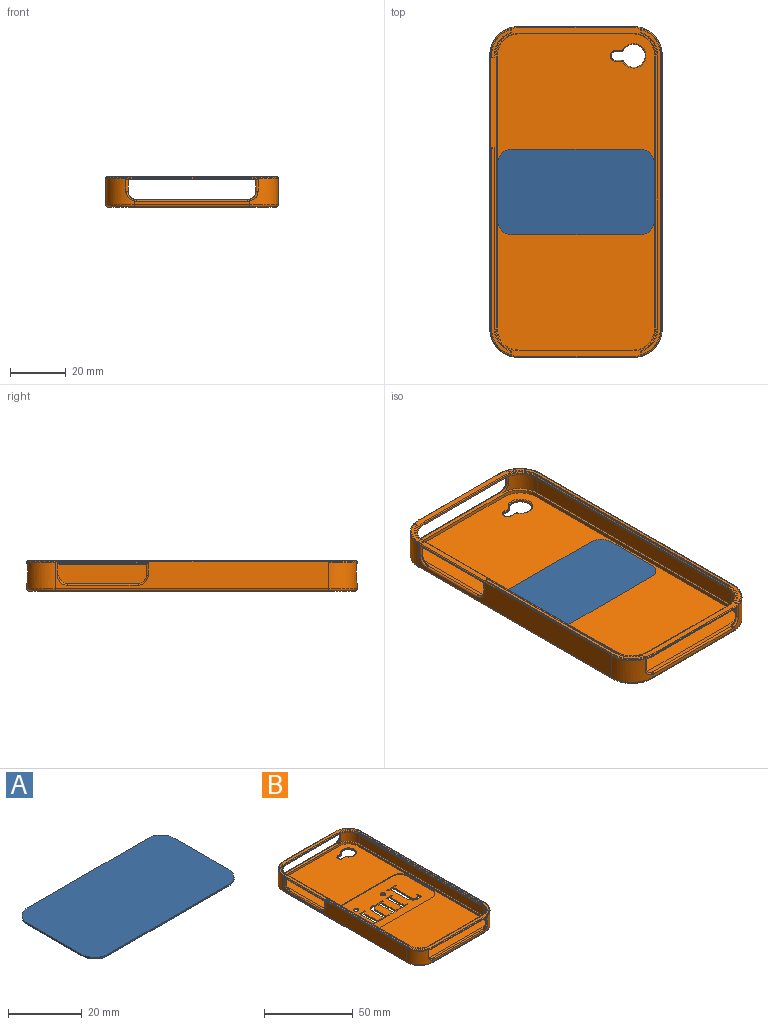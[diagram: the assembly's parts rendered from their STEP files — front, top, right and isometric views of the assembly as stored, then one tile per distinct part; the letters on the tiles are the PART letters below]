
ASSEMBLY  parts=2 mates=1
PART A: 94 faces, bbox 56.3x30.7x1.5 mm
  f0: plane 20.75x0.5mm, normal (-1,0,0), area 10.4mm2, adj f1,f7,f8,f9
  f1: cylinder r=5mm len=5mm, axis (0,0,-1), area 3.9mm2, adj f0,f2,f8,f9
  f2: plane 46.31x0.5mm, normal (0,-1,0), area 23.2mm2, adj f1,f3,f8,f9
  f3: cylinder r=5mm len=5mm, axis (0,0,-1), area 3.9mm2, adj f2,f4,f8,f9
  f4: plane 20.75x0.5mm, normal (1,0,0), area 10.4mm2, adj f3,f5,f8,f9
  f5: cylinder r=5mm len=5mm, axis (0,0,-1), area 3.9mm2, adj f4,f6,f8,f9
  f6: plane 46.31x0.5mm, normal (0,1,0), area 23.2mm2, adj f5,f7,f8,f9
  f7: cylinder r=5mm len=5mm, axis (0,0,-1), area 3.9mm2, adj f0,f6,f8,f9
  f8: plane 56.31x30.75mm, normal (0,0,1), area 1710.1mm2, adj f0,f1,f2,f3,f4,f5,f6,f7
  f9: plane 56.31x30.75mm, normal (0,0,-1), area 1506.8mm2, adj f0,f1,f2,f3,f4,f5,f6,f7
  f10: plane 2.31x1mm, normal (0.15,-0.99,0), area 2.3mm2, adj f9,f11,f26,f27
  f11: plane 13.54x1mm, normal (1,0,0), area 13.5mm2, adj f9,f10,f12,f27
  f12: extruded ~2.56x1.88mm, area 3.6mm2, adj f9,f11,f13,f27
  f13: extruded ~1.04x1mm, area 1.1mm2, adj f9,f12,f14,f27
  f14: extruded ~1x0.73mm, area 0.9mm2, adj f9,f13,f15,f27
  f15: plane 1.87x1mm, normal (-0.98,0.21,0), area 1.9mm2, adj f9,f14,f16,f27
  f16: plane 1x0.89mm, normal (0,1,0), area 0.9mm2, adj f9,f15,f17,f27
  f17: plane 3.29x1mm, normal (1,0,0), area 3.3mm2, adj f9,f16,f18,f27
  f18: extruded ~2.79x1mm, area 2.8mm2, adj f9,f17,f19,f27
  f19: extruded ~2.51x1mm, area 2.7mm2, adj f9,f18,f20,f27
  f20: extruded ~2.14x1.68mm, area 2.8mm2, adj f9,f19,f21,f27
  f21: extruded ~3.16x1mm, area 3.2mm2, adj f9,f20,f22,f27
  f22: plane 11.17x1mm, normal (-1,0,0), area 11.2mm2, adj f9,f21,f23,f27
  f23: plane 2.05x1mm, normal (-0.17,-0.99,0), area 2.1mm2, adj f9,f22,f24,f27
  f24: plane 1x0.72mm, normal (-1,0,0), area 0.7mm2, adj f9,f23,f25,f27
  f25: plane 6.94x1mm, normal (0,1,0), area 6.9mm2, adj f9,f24,f26,f27
  f26: plane 1x0.72mm, normal (1,0,0), area 0.7mm2, adj f9,f10,f25,f27
  f27: plane 18.32x9.57mm, normal (0,0,-1), area 55.1mm2, adj f10,f11,f12,f13,f14,f15,f16,f17
  f28: extruded ~1.03x1mm, area 1.1mm2, adj f9,f29,f35,f36
  f29: extruded ~1.04x1mm, area 1.2mm2, adj f9,f28,f30,f36
  f30: extruded ~1.03x1mm, area 1.2mm2, adj f9,f29,f31,f36
  f31: extruded ~1.03x1mm, area 1.1mm2, adj f9,f30,f32,f36
  f32: extruded ~1.04x1mm, area 1.2mm2, adj f9,f31,f33,f36
  f33: extruded ~1.03x1mm, area 1.1mm2, adj f9,f32,f34,f36
  f34: extruded ~1.03x1mm, area 1.1mm2, adj f9,f33,f35,f36
  f35: extruded ~1.03x1mm, area 1.2mm2, adj f9,f28,f34,f36
  f36: plane 2.92x2.92mm, normal (0,0,-1), area 6.7mm2, adj f28,f29,f30,f31,f32,f33,f34,f35
  f37: plane 2.17x1mm, normal (-0.15,0.99,0), area 2.2mm2, adj f9,f38,f46,f47
  f38: plane 11.71x1mm, normal (-1,0,0), area 11.7mm2, adj f9,f37,f39,f47
  f39: plane 4.02x1mm, normal (0,1,0), area 4mm2, adj f9,f38,f40,f47
  f40: plane 1x0.61mm, normal (1,0,0), area 0.6mm2, adj f9,f39,f41,f47
  f41: plane 1.79x1mm, normal (0.18,-0.98,0), area 1.8mm2, adj f9,f40,f42,f47
  f42: plane 10.77x1mm, normal (1,0,0), area 10.8mm2, adj f9,f41,f43,f47
  f43: plane 2.15x1mm, normal (0.15,0.99,0), area 2.2mm2, adj f9,f42,f44,f47
  f44: plane 1x0.61mm, normal (1,0,0), area 0.6mm2, adj f9,f43,f45,f47
  f45: plane 6.55x1mm, normal (0,-1,0), area 6.6mm2, adj f9,f44,f46,f47
  f46: plane 1x0.61mm, normal (-1,0,0), area 0.6mm2, adj f9,f37,f45,f47
  f47: plane 12.65x6.55mm, normal (0,0,-1), area 33mm2, adj f37,f38,f39,f40,f41,f42,f43,f44
  f48: extruded ~2.21x1mm, area 2.4mm2, adj f9,f49,f72,f73
  f49: plane 1.03x1mm, normal (-0.99,0.12,0), area 1mm2, adj f9,f48,f50,f73
  f50: plane 3.6x1mm, normal (0,1,0), area 3.6mm2, adj f9,f49,f51,f73
  f51: plane 1x0.61mm, normal (1,0,0), area 0.6mm2, adj f9,f50,f52,f73
  f52: plane 1.52x1mm, normal (0.22,-0.98,0), area 1.6mm2, adj f9,f51,f53,f73
  f53: plane 10.77x1mm, normal (1,0,0), area 10.8mm2, adj f9,f52,f54,f73
  f54: plane 1.52x1mm, normal (0.22,0.98,0), area 1.6mm2, adj f9,f53,f55,f73
  f55: plane 1x0.61mm, normal (1,0,0), area 0.6mm2, adj f9,f54,f56,f73
  f56: plane 5.46x1mm, normal (0,-1,0), area 5.5mm2, adj f9,f55,f57,f73
  f57: plane 1x0.61mm, normal (-1,0,0), area 0.6mm2, adj f9,f56,f58,f73
  f58: plane 1.71x1mm, normal (-0.19,0.98,0), area 1.7mm2, adj f9,f57,f59,f73
  f59: plane 10.08x1mm, normal (-1,0,0), area 10.1mm2, adj f9,f58,f60,f73
  f60: extruded ~2.97x1mm, area 3mm2, adj f9,f59,f61,f73
  f61: extruded ~1.69x1mm, area 1.9mm2, adj f9,f60,f62,f73
  f62: extruded ~1.76x1mm, area 1.9mm2, adj f9,f61,f63,f73
  f63: plane 8.07x1mm, normal (1,0,0), area 8.1mm2, adj f9,f62,f64,f73
  f64: plane 1.68x1mm, normal (0.2,0.98,0), area 1.7mm2, adj f9,f63,f65,f73
  f65: plane 1x0.61mm, normal (1,0,0), area 0.6mm2, adj f9,f64,f66,f73
  f66: plane 5.45x1mm, normal (0,-1,0), area 5.4mm2, adj f9,f65,f67,f73
  f67: plane 1x0.61mm, normal (-1,0,0), area 0.6mm2, adj f9,f66,f68,f73
  f68: plane 1.53x1mm, normal (-0.21,0.98,0), area 1.6mm2, adj f9,f67,f69,f73
  f69: plane 8.32x1mm, normal (-1,0,0), area 8.3mm2, adj f9,f68,f70,f73
  f70: extruded ~2.77x1mm, area 3mm2, adj f9,f69,f71,f73
  f71: extruded ~2.48x1mm, area 2.7mm2, adj f9,f70,f72,f73
  f72: extruded ~1.95x1mm, area 2mm2, adj f9,f48,f71,f73
  f73: plane 12.99x12.73mm, normal (0,0,-1), area 68.8mm2, adj f48,f49,f50,f51,f52,f53,f54,f55
  f74: extruded ~1.03x1mm, area 1.1mm2, adj f9,f75,f81,f82
  f75: extruded ~1.04x1mm, area 1.2mm2, adj f9,f74,f76,f82
  f76: extruded ~1.03x1mm, area 1.2mm2, adj f9,f75,f77,f82
  f77: extruded ~1.03x1mm, area 1.1mm2, adj f9,f76,f78,f82
  f78: extruded ~1.04x1mm, area 1.2mm2, adj f9,f77,f79,f82
  f79: extruded ~1.03x1mm, area 1.1mm2, adj f9,f78,f80,f82
  f80: extruded ~1.03x1mm, area 1.1mm2, adj f9,f79,f81,f82
  f81: extruded ~1.03x1mm, area 1.2mm2, adj f9,f74,f80,f82
  f82: plane 2.92x2.92mm, normal (0,0,-1), area 6.7mm2, adj f74,f75,f76,f77,f78,f79,f80,f81
  f83: plane 2.17x1mm, normal (-0.15,0.99,0), area 2.2mm2, adj f9,f84,f92,f93
  f84: plane 11.71x1mm, normal (-1,0,0), area 11.7mm2, adj f9,f83,f85,f93
  f85: plane 4.02x1mm, normal (0,1,0), area 4mm2, adj f9,f84,f86,f93
  f86: plane 1x0.61mm, normal (1,0,0), area 0.6mm2, adj f9,f85,f87,f93
  f87: plane 1.79x1mm, normal (0.18,-0.98,0), area 1.8mm2, adj f9,f86,f88,f93
  f88: plane 10.77x1mm, normal (1,0,0), area 10.8mm2, adj f9,f87,f89,f93
  f89: plane 2.15x1mm, normal (0.15,0.99,0), area 2.2mm2, adj f9,f88,f90,f93
  f90: plane 1x0.61mm, normal (1,0,0), area 0.6mm2, adj f9,f89,f91,f93
  f91: plane 6.55x1mm, normal (0,-1,0), area 6.6mm2, adj f9,f90,f92,f93
  f92: plane 1x0.61mm, normal (-1,0,0), area 0.6mm2, adj f9,f83,f91,f93
  f93: plane 12.65x6.55mm, normal (0,0,-1), area 33mm2, adj f83,f84,f85,f86,f87,f88,f89,f90
PART B: 324 faces, bbox 64x121x11.4 mm
  f0: cylinder r=10.5mm len=3.15mm, axis (0,0,-1), area 1.2mm2, adj f34,f36,f230,f279,f281,f317
  f1: cylinder r=10.5mm len=2.71mm, axis (0,0,-1), area 0.2mm2, adj f23,f83,f288,f290
  f2: cylinder r=10.5mm len=2.71mm, axis (0,0,-1), area 0.2mm2, adj f43,f86,f295,f297
  f3: cylinder r=10.5mm len=3.15mm, axis (0,0,-1), area 1.2mm2, adj f44,f50,f229,f304,f306,f322
  f4: plane 118.56x60.05mm, normal (0,0,1), area 347.8mm2, adj f243,f245,f247,f249,f250,f251,f252,f253
  f5: plane 0.63x0.29mm, normal (1,0,0), area 0.2mm2, adj f7,f19,f60,f241
  f6: cylinder r=8.22mm len=7.73mm, axis (0,0,-1), area 2.9mm2, adj f11,f29,f30,f91,f241
  f7: cylinder r=8.22mm len=7.73mm, axis (0,0,-1), area 2.9mm2, adj f5,f16,f18,f92,f241
  f8: plane 64.93x0.29mm, normal (1,0,0), area 18.8mm2, adj f9,f31,f90,f241
  f9: cylinder r=8.22mm len=7.73mm, axis (0,0,-1), area 2.9mm2, adj f8,f38,f41,f88,f241
  f10: cylinder r=8.22mm len=7.73mm, axis (0,0,-1), area 2.9mm2, adj f11,f39,f42,f87,f241
  f11: plane 98.26x0.29mm, normal (-1,0,0), area 28.5mm2, adj f6,f10,f89,f241
  f12: plane 4.2x0.05mm, normal (0,-1,0), area 0.2mm2, adj f14,f26,f98,f241
  f13: plane 4.2x0.05mm, normal (0,1,0), area 0.2mm2, adj f25,f35,f97,f241
  f14: cylinder r=0.6mm len=4.2mm, axis (0,0,-1), area 3.7mm2, adj f12,f15,f58,f120,f241
  f15: cylinder r=0.6mm len=0.79mm, axis (-1,0,0), area 0.4mm2, adj f14,f17,f59,f241
  f16: cylinder r=0.6mm len=0.35mm, axis (0,0,-1), area 0.1mm2, adj f7,f18,f241
  f17: cylinder r=0.6mm len=0.71mm, axis (-0.97,0,-0.24), area 0.3mm2, adj f15,f19,f60,f241
  f18: cylinder r=0.6mm len=0.73mm, axis (0,0.97,-0.23), area 0.3mm2, adj f7,f16,f21,f92,f241
  f19: cylinder r=0.6mm len=0.55mm, axis (0,0,-1), area 0.1mm2, adj f5,f17,f241
  f20: cylinder r=0.6mm len=4.2mm, axis (0,0,-1), area 3.1mm2, adj f21,f24,f74,f121,f241
  f21: cylinder r=0.6mm len=0.9mm, axis (0,-1,0), area 0.5mm2, adj f18,f20,f59,f74,f92,f241
  f22: sphere r=0.6mm, area 0.1mm2, adj f23,f24,f231,f282
  f23: torus R=9.67mm, axis (0,0,1), area 3.8mm2, adj f1,f22,f82,f284,f286
  f24: cylinder r=0.6mm len=4.66mm, axis (0,0,-1), area 4.8mm2, adj f20,f22,f82,f123,f231,f241,f319
  f25: cylinder r=0.6mm len=4.2mm, axis (0,0,1), area 3.7mm2, adj f13,f27,f75,f122,f241
  f26: cylinder r=0.6mm len=4.5mm, axis (0,0,1), area 4.1mm2, adj f12,f83,f126,f241,f323
  f27: cylinder r=0.6mm len=0.79mm, axis (1,0,0), area 0.4mm2, adj f25,f28,f79,f241
  f28: cylinder r=0.6mm len=0.71mm, axis (0.97,0,0.24), area 0.3mm2, adj f27,f31,f90,f241
  f29: cylinder r=0.6mm len=0.35mm, axis (0,0,-1), area 0.1mm2, adj f6,f30,f241
  f30: cylinder r=0.6mm len=0.73mm, axis (0,0.97,-0.23), area 0.3mm2, adj f6,f29,f32,f91,f241
  f31: cylinder r=0.6mm len=0.55mm, axis (0,0,-1), area 0.1mm2, adj f8,f28,f241
  f32: cylinder r=0.6mm len=0.9mm, axis (0,1,0), area 0.5mm2, adj f30,f33,f61,f73,f91,f241
  f33: cylinder r=0.6mm len=4.2mm, axis (0,0,-1), area 3.1mm2, adj f32,f34,f73,f127,f241
  f34: cylinder r=0.6mm len=4.66mm, axis (0,0,-1), area 4.8mm2, adj f0,f33,f36,f81,f130,f241,f317
  f35: cylinder r=0.6mm len=4.5mm, axis (0,0,1), area 4.1mm2, adj f13,f83,f131,f241,f323
  f36: sphere r=0.6mm, area 0.1mm2, adj f0,f34,f37,f283
  f37: torus R=9.67mm, axis (0,0,1), area 3.8mm2, adj f36,f81,f228,f285,f287
  f38: cylinder r=0.6mm len=0.35mm, axis (0,0,-1), area 0.1mm2, adj f9,f41,f241
  f39: cylinder r=0.6mm len=0.35mm, axis (0,0,-1), area 0.1mm2, adj f10,f42,f241
  f40: torus R=9.67mm, axis (0,0,1), area 3.8mm2, adj f44,f84,f226,f298,f300
  f41: cylinder r=0.6mm len=0.73mm, axis (0,-0.97,-0.23), area 0.3mm2, adj f9,f38,f45,f88,f241
  f42: cylinder r=0.6mm len=0.73mm, axis (0,-0.97,-0.23), area 0.3mm2, adj f10,f39,f48,f87,f241
  f43: torus R=9.67mm, axis (0,0,1), area 3.8mm2, adj f2,f49,f85,f299,f301
  f44: sphere r=0.6mm, area 0.1mm2, adj f3,f40,f50,f302
  f45: cylinder r=0.6mm len=0.9mm, axis (0,-1,0), area 0.5mm2, adj f41,f46,f76,f79,f88,f241
  f46: cylinder r=0.6mm len=4.2mm, axis (0,0,-1), area 3.1mm2, adj f45,f50,f76,f132,f241
  f47: cylinder r=0.6mm len=4.2mm, axis (0,0,-1), area 3.1mm2, adj f48,f51,f77,f133,f241
  f48: cylinder r=0.6mm len=0.9mm, axis (0,1,0), area 0.5mm2, adj f42,f47,f61,f77,f87,f241
  f49: sphere r=0.6mm, area 0.1mm2, adj f43,f51,f227,f303
  f50: cylinder r=0.6mm len=4.66mm, axis (0,0,-1), area 4.8mm2, adj f3,f44,f46,f84,f134,f241,f322
  f51: cylinder r=0.6mm len=4.66mm, axis (0,0,-1), area 4.8mm2, adj f47,f49,f85,f135,f227,f241,f320
  f52: plane 114.7x57.95mm, normal (0,0,1), area 4802.7mm2, adj f53,f54,f55,f65,f66,f67,f68,f69
  f53: torus R=4.43mm, axis (0,0,1), area 12.7mm2, adj f52,f102,f118,f119
  f54: torus R=1.93mm, axis (0,0,1), area 3.1mm2, adj f52,f55,f57,f117
  f55: cylinder r=0.3mm len=2.17mm, axis (1,0,0), area 1.2mm2, adj f52,f54,f101,f119
  f56: torus R=5.04mm, axis (0,0,1), area 20.8mm2, adj f80,f102,f112,f113
  f57: cone r=1.5mm half-angle=20deg, axis (0,0,-1), area 3.8mm2, adj f54,f99,f101,f116
  f58: plane 6.76x2.59mm, normal (1,0,0), area 8.1mm2, adj f14,f59,f64,f74,f120
  f59: plane 9.36x6.18mm, normal (0,0,-1), area 5.2mm2, adj f15,f21,f58,f60,f74,f92
  f60: plane 0.63x0.6mm, normal (0.24,0,-0.97), area 0.4mm2, adj f5,f17,f59,f92
  f61: plane 115.71x6.18mm, normal (0,0,-1), area 44.3mm2, adj f32,f48,f73,f77,f78,f87,f89,f91
  f62: plane 41.51x1.28mm, normal (0,1,0), area 49.9mm2, adj f81,f82,f105,f124,f125,f128
  f63: plane 41.51x1.28mm, normal (0,-1,0), area 49.9mm2, adj f84,f85,f110,f136,f137,f138
  f64: plane 118.1x60.5mm, normal (0,0,1), area 353.7mm2, adj f58,f65,f66,f67,f68,f69,f70,f71
  f65: cylinder r=8.22mm len=8.22mm, axis (0,0,-1), area 16.8mm2, adj f52,f64,f66,f72
  f66: plane 41.51x1.3mm, normal (0,1,0), area 54mm2, adj f52,f64,f65,f67
  f67: cylinder r=8.22mm len=8.22mm, axis (0,0,-1), area 16.8mm2, adj f52,f64,f66,f68
  f68: plane 98.26x1.3mm, normal (-1,0,0), area 127.7mm2, adj f52,f64,f67,f69
  f69: cylinder r=8.22mm len=8.22mm, axis (0,0,-1), area 16.8mm2, adj f52,f64,f68,f70
  f70: plane 41.51x1.3mm, normal (0,-1,0), area 54mm2, adj f52,f64,f69,f71
  f71: cylinder r=8.22mm len=8.22mm, axis (0,0,-1), area 16.8mm2, adj f52,f64,f70,f72
  f72: plane 98.26x1.3mm, normal (1,0,0), area 127.7mm2, adj f52,f64,f65,f71
  f73: cylinder r=8.77mm len=8.72mm, axis (0,0,-1), area 77.9mm2, adj f32,f33,f61,f64,f78,f127
  f74: cylinder r=8.77mm len=8.72mm, axis (0,0,-1), area 77.9mm2, adj f20,f21,f58,f59,f64,f121
  f75: plane 66.89x6.76mm, normal (1,0,0), area 442.7mm2, adj f25,f64,f76,f79,f122
  f76: cylinder r=8.77mm len=8.72mm, axis (0,0,-1), area 77.9mm2, adj f45,f46,f64,f75,f79,f132
  f77: cylinder r=8.77mm len=8.72mm, axis (0,0,-1), area 77.9mm2, adj f47,f48,f61,f64,f78,f133
  f78: plane 98.96x6.76mm, normal (-1,0,0), area 669mm2, adj f61,f64,f73,f77
  f79: plane 73.66x6.18mm, normal (0,0,-1), area 27.7mm2, adj f27,f45,f75,f76,f88,f90
  f80: plane 117x60.05mm, normal (0,0,-1), area 6650.4mm2, adj f56,f104,f105,f106,f107,f108,f109,f110
  f81: cylinder r=10.27mm len=10.27mm, axis (0,0,-1), area 130.3mm2, adj f34,f37,f62,f86,f104,f130
  f82: cylinder r=10.27mm len=10.27mm, axis (0,0,-1), area 130.3mm2, adj f23,f24,f62,f83,f107,f123
  f83: plane 98.47x9.71mm, normal (-1,0,0), area 695.6mm2, adj f1,f26,f35,f82,f84,f109,f126,f129
  f84: cylinder r=10.27mm len=10.27mm, axis (0,0,-1), area 130.3mm2, adj f40,f50,f63,f83,f111,f134
  f85: cylinder r=10.27mm len=10.27mm, axis (0,0,-1), area 130.3mm2, adj f43,f51,f63,f86,f108,f135
  f86: plane 98.47x9.71mm, normal (1,0,0), area 955mm2, adj f2,f81,f85,f106,f228,f293
  f87: cone r=8.82mm half-angle=76deg, axis (0,0,-1), area 6.4mm2, adj f10,f42,f48,f61,f89
  f88: cone r=8.82mm half-angle=76deg, axis (0,0,-1), area 6.4mm2, adj f9,f41,f45,f79,f90
  f89: plane 98.26x0.6mm, normal (-0.24,0,-0.97), area 60.8mm2, adj f11,f61,f87,f91
  f90: plane 64.93x0.6mm, normal (0.24,0,-0.97), area 40.2mm2, adj f8,f28,f79,f88
  f91: cone r=8.82mm half-angle=76deg, axis (0,0,-1), area 6.4mm2, adj f6,f30,f32,f61,f89
  f92: cone r=8.82mm half-angle=76deg, axis (0,0,-1), area 6.4mm2, adj f7,f18,f21,f59,f60
  f93: cylinder r=3mm len=2.53mm, axis (0,-1,0), area 0.1mm2, adj f64,f127,f128,f130
  f94: cylinder r=3mm len=2.53mm, axis (0,1,0), area 0.1mm2, adj f64,f121,f123,f124
  f95: cylinder r=3mm len=2.53mm, axis (0,-1,0), area 0.1mm2, adj f64,f133,f135,f137
  f96: cylinder r=3mm len=2.53mm, axis (0,1,0), area 0.1mm2, adj f64,f132,f134,f136
  f97: cylinder r=3mm len=3mm, axis (-1,0,0), area 0.2mm2, adj f13,f64,f122,f131
  f98: cylinder r=3mm len=3mm, axis (1,0,0), area 0.2mm2, adj f12,f64,f120,f126
  f99: plane 2.17x0.64mm, normal (0,-0.94,-0.34), area 1.5mm2, adj f57,f100,f114,f117
  f100: cone r=0.45mm half-angle=20deg, axis (0,0,1), area 0.5mm2, adj f99,f102,f112,f118
  f101: plane 2.17x0.64mm, normal (0,0.94,-0.34), area 1.5mm2, adj f55,f57,f103,f115
  f102: cone r=4mm half-angle=20deg, axis (0,0,-1), area 15.1mm2, adj f53,f56,f100,f103
  f103: cone r=0.45mm half-angle=20deg, axis (0,0,1), area 0.5mm2, adj f101,f102,f113,f119
  f104: torus R=9.27mm, axis (0,0,1), area 24.4mm2, adj f80,f81,f105,f106
  f105: cylinder r=1mm len=41.51mm, axis (-1,0,0), area 65.2mm2, adj f62,f80,f104,f107
  f106: cylinder r=1mm len=98.46mm, axis (0,1,0), area 154.7mm2, adj f80,f86,f104,f108
  f107: torus R=9.27mm, axis (0,0,1), area 24.4mm2, adj f80,f82,f105,f109
  f108: torus R=9.27mm, axis (0,0,1), area 24.4mm2, adj f80,f85,f106,f110
  f109: cylinder r=1mm len=98.46mm, axis (0,-1,0), area 154.7mm2, adj f80,f83,f107,f111
  f110: cylinder r=1mm len=41.51mm, axis (1,0,0), area 65.2mm2, adj f63,f80,f108,f111
  f111: torus R=9.27mm, axis (0,0,1), area 24.4mm2, adj f80,f84,f109,f110
  f112: bspline ~0.66x0.56mm, area 0.2mm2, adj f56,f100,f114
  f113: bspline ~0.66x0.56mm, area 0.2mm2, adj f56,f103,f115
  f114: cylinder r=0.7mm len=2.17mm, axis (-1,0,0), area 1.8mm2, adj f80,f99,f112,f116
  f115: cylinder r=0.7mm len=2.17mm, axis (1,0,0), area 1.8mm2, adj f80,f101,f113,f116
  f116: torus R=2.54mm, axis (0,0,1), area 5.8mm2, adj f57,f80,f114,f115
  f117: cylinder r=0.3mm len=2.17mm, axis (-1,0,0), area 1.2mm2, adj f52,f54,f99,f118
  f118: torus R=0.57mm, axis (0,0,1), area 0.5mm2, adj f52,f53,f100,f117
  f119: torus R=0.57mm, axis (0,0,1), area 0.5mm2, adj f52,f53,f55,f103
  f120: torus R=3.6mm, axis (1,0,0), area 3.8mm2, adj f14,f58,f64,f98
  f121: bspline ~3.6x3.46mm, area 3.4mm2, adj f20,f64,f74,f94,f123
  f122: torus R=3.6mm, axis (1,0,0), area 3.8mm2, adj f25,f64,f75,f97
  f123: bspline ~3.52x3.15mm, area 4.6mm2, adj f24,f82,f94,f121,f124
  f124: torus R=3.6mm, axis (0,-1,0), area 0.6mm2, adj f62,f94,f123,f125
  f125: cylinder r=0.6mm len=40mm, axis (1,0,0), area 37.7mm2, adj f62,f64,f124,f128
  f126: torus R=3.6mm, axis (1,0,0), area 4.8mm2, adj f26,f83,f98,f129
  f127: bspline ~3.6x3.46mm, area 3.4mm2, adj f33,f64,f73,f93,f130
  f128: torus R=3.6mm, axis (0,-1,0), area 0.6mm2, adj f62,f93,f125,f130
  f129: cylinder r=0.6mm len=25.5mm, axis (0,-1,0), area 24mm2, adj f64,f83,f126,f131
  f130: bspline ~3.52x3.15mm, area 4.6mm2, adj f34,f81,f93,f127,f128
  f131: torus R=3.6mm, axis (1,0,0), area 4.8mm2, adj f35,f83,f97,f129
  f132: bspline ~3.6x3.46mm, area 3.4mm2, adj f46,f64,f76,f96,f134
  f133: bspline ~3.6x3.46mm, area 3.4mm2, adj f47,f64,f77,f95,f135
  f134: bspline ~3.52x3.15mm, area 4.6mm2, adj f50,f84,f96,f132,f136
  f135: bspline ~3.52x3.15mm, area 4.6mm2, adj f51,f85,f95,f133,f137
  f136: torus R=3.6mm, axis (0,1,0), area 0.6mm2, adj f63,f96,f134,f138
  f137: torus R=3.6mm, axis (0,1,0), area 0.6mm2, adj f63,f95,f135,f138
  f138: cylinder r=0.6mm len=40mm, axis (-1,0,0), area 37.7mm2, adj f63,f64,f136,f137
  f139: plane 20.75x0.5mm, normal (1,0,0), area 10.4mm2, adj f52,f140,f146,f147
  f140: cylinder r=5mm len=5mm, axis (0,0,-1), area 3.9mm2, adj f52,f139,f141,f147
  f141: plane 46.31x0.5mm, normal (0,1,0), area 23.2mm2, adj f52,f140,f142,f147
  f142: cylinder r=5mm len=5mm, axis (0,0,-1), area 3.9mm2, adj f52,f141,f143,f147
  f143: plane 20.75x0.5mm, normal (-1,0,0), area 10.4mm2, adj f52,f142,f144,f147
  f144: cylinder r=5mm len=5mm, axis (0,0,-1), area 3.9mm2, adj f52,f143,f145,f147
  f145: plane 46.31x0.5mm, normal (0,-1,0), area 23.2mm2, adj f52,f144,f146,f147
  f146: cylinder r=5mm len=5mm, axis (0,0,-1), area 3.9mm2, adj f52,f139,f145,f147
  f147: plane 56.31x30.75mm, normal (0,0,1), area 1506.8mm2, adj f139,f140,f141,f142,f143,f144,f145,f146
  f148: plane 2.31x1mm, normal (-0.15,0.99,0), area 2.3mm2, adj f80,f147,f149,f164
  f149: plane 13.54x1mm, normal (-1,0,0), area 13.5mm2, adj f80,f147,f148,f150
  f150: extruded ~2.56x1.88mm, area 3.6mm2, adj f80,f147,f149,f151
  f151: extruded ~1.04x1mm, area 1.1mm2, adj f80,f147,f150,f152
  f152: extruded ~1x0.73mm, area 0.9mm2, adj f80,f147,f151,f153
  f153: plane 1.87x1mm, normal (0.98,-0.21,0), area 1.9mm2, adj f80,f147,f152,f154
  f154: plane 1x0.89mm, normal (0,-1,0), area 0.9mm2, adj f80,f147,f153,f155
  f155: plane 3.29x1mm, normal (-1,0,0), area 3.3mm2, adj f80,f147,f154,f156
  f156: extruded ~2.79x1mm, area 2.8mm2, adj f80,f147,f155,f157
  f157: extruded ~2.51x1mm, area 2.7mm2, adj f80,f147,f156,f158
  f158: extruded ~2.14x1.68mm, area 2.8mm2, adj f80,f147,f157,f159
  f159: extruded ~3.16x1mm, area 3.2mm2, adj f80,f147,f158,f160
  f160: plane 11.17x1mm, normal (1,0,0), area 11.2mm2, adj f80,f147,f159,f161
  f161: plane 2.05x1mm, normal (0.17,0.99,0), area 2.1mm2, adj f80,f147,f160,f162
  f162: plane 1x0.72mm, normal (1,0,0), area 0.7mm2, adj f80,f147,f161,f163
  f163: plane 6.94x1mm, normal (0,-1,0), area 6.9mm2, adj f80,f147,f162,f164
  f164: plane 1x0.72mm, normal (-1,0,0), area 0.7mm2, adj f80,f147,f148,f163
  f165: extruded ~1.03x1mm, area 1.1mm2, adj f80,f147,f166,f172
  f166: extruded ~1.04x1mm, area 1.2mm2, adj f80,f147,f165,f167
  f167: extruded ~1.03x1mm, area 1.2mm2, adj f80,f147,f166,f168
  f168: extruded ~1.03x1mm, area 1.1mm2, adj f80,f147,f167,f169
  f169: extruded ~1.04x1mm, area 1.2mm2, adj f80,f147,f168,f170
  f170: extruded ~1.03x1mm, area 1.1mm2, adj f80,f147,f169,f171
  f171: extruded ~1.03x1mm, area 1.1mm2, adj f80,f147,f170,f172
  f172: extruded ~1.03x1mm, area 1.2mm2, adj f80,f147,f165,f171
  f173: plane 2.17x1mm, normal (0.15,-0.99,0), area 2.2mm2, adj f80,f147,f174,f182
  f174: plane 11.71x1mm, normal (1,0,0), area 11.7mm2, adj f80,f147,f173,f175
  f175: plane 4.02x1mm, normal (0,-1,0), area 4mm2, adj f80,f147,f174,f176
  f176: plane 1x0.61mm, normal (-1,0,0), area 0.6mm2, adj f80,f147,f175,f177
  f177: plane 1.79x1mm, normal (-0.18,0.98,0), area 1.8mm2, adj f80,f147,f176,f178
  f178: plane 10.77x1mm, normal (-1,0,0), area 10.8mm2, adj f80,f147,f177,f179
  f179: plane 2.15x1mm, normal (-0.15,-0.99,0), area 2.2mm2, adj f80,f147,f178,f180
  f180: plane 1x0.61mm, normal (-1,0,0), area 0.6mm2, adj f80,f147,f179,f181
  f181: plane 6.55x1mm, normal (0,1,0), area 6.6mm2, adj f80,f147,f180,f182
  f182: plane 1x0.61mm, normal (1,0,0), area 0.6mm2, adj f80,f147,f173,f181
  f183: extruded ~2.21x1mm, area 2.4mm2, adj f80,f147,f184,f207
  f184: plane 1.03x1mm, normal (0.99,-0.12,0), area 1mm2, adj f80,f147,f183,f185
  f185: plane 3.6x1mm, normal (0,-1,0), area 3.6mm2, adj f80,f147,f184,f186
  f186: plane 1x0.61mm, normal (-1,0,0), area 0.6mm2, adj f80,f147,f185,f187
  f187: plane 1.52x1mm, normal (-0.22,0.98,0), area 1.6mm2, adj f80,f147,f186,f188
  f188: plane 10.77x1mm, normal (-1,0,0), area 10.8mm2, adj f80,f147,f187,f189
  f189: plane 1.52x1mm, normal (-0.22,-0.98,0), area 1.6mm2, adj f80,f147,f188,f190
  f190: plane 1x0.61mm, normal (-1,0,0), area 0.6mm2, adj f80,f147,f189,f191
  f191: plane 5.46x1mm, normal (0,1,0), area 5.5mm2, adj f80,f147,f190,f192
  f192: plane 1x0.61mm, normal (1,0,0), area 0.6mm2, adj f80,f147,f191,f193
  f193: plane 1.71x1mm, normal (0.19,-0.98,0), area 1.7mm2, adj f80,f147,f192,f194
  f194: plane 10.08x1mm, normal (1,0,0), area 10.1mm2, adj f80,f147,f193,f195
  f195: extruded ~2.97x1mm, area 3mm2, adj f80,f147,f194,f196
  f196: extruded ~1.69x1mm, area 1.9mm2, adj f80,f147,f195,f197
  f197: extruded ~1.76x1mm, area 1.9mm2, adj f80,f147,f196,f198
  f198: plane 8.07x1mm, normal (-1,0,0), area 8.1mm2, adj f80,f147,f197,f199
  f199: plane 1.68x1mm, normal (-0.2,-0.98,0), area 1.7mm2, adj f80,f147,f198,f200
  f200: plane 1x0.61mm, normal (-1,0,0), area 0.6mm2, adj f80,f147,f199,f201
  f201: plane 5.45x1mm, normal (0,1,0), area 5.4mm2, adj f80,f147,f200,f202
  f202: plane 1x0.61mm, normal (1,0,0), area 0.6mm2, adj f80,f147,f201,f203
  f203: plane 1.53x1mm, normal (0.21,-0.98,0), area 1.6mm2, adj f80,f147,f202,f204
  f204: plane 8.32x1mm, normal (1,0,0), area 8.3mm2, adj f80,f147,f203,f205
  f205: extruded ~2.77x1mm, area 3mm2, adj f80,f147,f204,f206
  f206: extruded ~2.48x1mm, area 2.7mm2, adj f80,f147,f205,f207
  f207: extruded ~1.95x1mm, area 2mm2, adj f80,f147,f183,f206
  f208: extruded ~1.03x1mm, area 1.1mm2, adj f80,f147,f209,f215
  f209: extruded ~1.04x1mm, area 1.2mm2, adj f80,f147,f208,f210
  f210: extruded ~1.03x1mm, area 1.2mm2, adj f80,f147,f209,f211
  f211: extruded ~1.03x1mm, area 1.1mm2, adj f80,f147,f210,f212
  f212: extruded ~1.04x1mm, area 1.2mm2, adj f80,f147,f211,f213
  f213: extruded ~1.03x1mm, area 1.1mm2, adj f80,f147,f212,f214
  f214: extruded ~1.03x1mm, area 1.1mm2, adj f80,f147,f213,f215
  f215: extruded ~1.03x1mm, area 1.2mm2, adj f80,f147,f208,f214
  f216: plane 2.17x1mm, normal (0.15,-0.99,0), area 2.2mm2, adj f80,f147,f217,f225
  f217: plane 11.71x1mm, normal (1,0,0), area 11.7mm2, adj f80,f147,f216,f218
  f218: plane 4.02x1mm, normal (0,-1,0), area 4mm2, adj f80,f147,f217,f219
  f219: plane 1x0.61mm, normal (-1,0,0), area 0.6mm2, adj f80,f147,f218,f220
  f220: plane 1.79x1mm, normal (-0.18,0.98,0), area 1.8mm2, adj f80,f147,f219,f221
  f221: plane 10.77x1mm, normal (-1,0,0), area 10.8mm2, adj f80,f147,f220,f222
  f222: plane 2.15x1mm, normal (-0.15,-0.99,0), area 2.2mm2, adj f80,f147,f221,f223
  f223: plane 1x0.61mm, normal (-1,0,0), area 0.6mm2, adj f80,f147,f222,f224
  f224: plane 6.55x1mm, normal (0,1,0), area 6.6mm2, adj f80,f147,f223,f225
  f225: plane 1x0.61mm, normal (1,0,0), area 0.6mm2, adj f80,f147,f216,f224
  f226: cylinder r=10.5mm len=2.71mm, axis (0,0,-1), area 0.2mm2, adj f40,f83,f294,f296
  f227: cylinder r=10.5mm len=3.15mm, axis (0,0,-1), area 1.2mm2, adj f49,f51,f229,f305,f307,f320
  f228: cylinder r=10.5mm len=2.71mm, axis (0,0,-1), area 0.2mm2, adj f37,f86,f289,f291
  f229: plane 41.05x0.4mm, normal (0,-1,0), area 16.4mm2, adj f3,f227,f308,f321
  f230: plane 41.05x0.4mm, normal (0,1,0), area 16.4mm2, adj f0,f231,f277,f318
  f231: cylinder r=10.5mm len=3.15mm, axis (0,0,-1), area 1.2mm2, adj f22,f24,f230,f278,f280,f319
  f232: cylinder r=8mm len=8mm, axis (0,0,-1), area 8.8mm2, adj f233,f239,f241,f313
  f233: plane 97.8x0.7mm, normal (-1,0,0), area 68.5mm2, adj f232,f234,f241,f315
  f234: cylinder r=8mm len=8mm, axis (0,0,-1), area 8.8mm2, adj f233,f235,f241,f316
  f235: plane 40.85x0.7mm, normal (0,1,0), area 28.6mm2, adj f234,f236,f241,f314
  f236: cylinder r=8mm len=8mm, axis (0,0,-1), area 8.8mm2, adj f235,f237,f241,f312
  f237: plane 97.8x0.7mm, normal (1,0,0), area 68.5mm2, adj f236,f238,f241,f310
  f238: cylinder r=8mm len=8mm, axis (0,0,-1), area 8.8mm2, adj f237,f239,f241,f309
  f239: plane 40.85x0.7mm, normal (0,-1,0), area 28.6mm2, adj f232,f238,f241,f311
  f240: plane 101.94x0.19mm, normal (0,0,1), area 3.8mm2, adj f244,f246,f248,f291,f293,f295
  f241: plane 118.4x59.55mm, normal (0,0,-1), area 370.6mm2, adj f5,f6,f7,f8,f9,f10,f11,f12
  f242: plane 116.94x6.83mm, normal (0,0,1), area 121.9mm2, adj f244,f245,f246,f248,f249,f251,f252,f253
  f243: sphere r=0.6mm, area 0.1mm2, adj f4,f244,f245,f301,f303,f305
  f244: torus R=9.67mm, axis (0,0,1), area 3.4mm2, adj f240,f242,f243,f246,f297,f299
  f245: cylinder r=0.6mm len=1.05mm, axis (0,-1,0), area 0.3mm2, adj f4,f242,f243,f247
  f246: cylinder r=0.6mm len=98.46mm, axis (0,-1,0), area 26.6mm2, adj f240,f242,f244,f248
  f247: sphere r=0.6mm, area 0mm2, adj f4,f245,f249
  f248: torus R=9.67mm, axis (0,0,1), area 3.4mm2, adj f240,f242,f246,f250,f287,f289
  f249: torus R=8.82mm, axis (0,0,1), area 2.9mm2, adj f4,f242,f247,f251
  f250: sphere r=0.6mm, area 0.1mm2, adj f4,f248,f252,f281,f283,f285
  f251: cylinder r=0.6mm len=98.26mm, axis (0,1,0), area 26.6mm2, adj f4,f242,f249,f253
  f252: cylinder r=0.6mm len=1.05mm, axis (0,-1,0), area 0.3mm2, adj f4,f242,f250,f254
  f253: torus R=8.82mm, axis (0,0,1), area 2.9mm2, adj f4,f242,f251,f254
  f254: sphere r=0.6mm, area 0mm2, adj f4,f252,f253
  f255: plane 74.27x6.83mm, normal (0,0,1), area 76.7mm2, adj f257,f258,f260,f261,f263,f264
  f256: sphere r=0.6mm, area 0.1mm2, adj f4,f257,f258,f300,f302,f304
  f257: cylinder r=0.6mm len=1.05mm, axis (0,1,0), area 0.3mm2, adj f4,f255,f256,f259
  f258: torus R=9.67mm, axis (0,0,1), area 3.4mm2, adj f4,f255,f256,f260,f296,f298
  f259: sphere r=0.6mm, area 0mm2, adj f4,f257,f261
  f260: cylinder r=0.6mm len=65.03mm, axis (0,1,0), area 17.6mm2, adj f4,f255,f258,f262
  f261: torus R=8.82mm, axis (0,0,1), area 2.9mm2, adj f4,f255,f259,f263
  f262: sphere r=0.6mm, area 0mm2, adj f4,f260,f264
  f263: cylinder r=0.6mm len=64.93mm, axis (0,-1,0), area 17.6mm2, adj f4,f255,f261,f265
  f264: cylinder r=0.6mm len=1mm, axis (-1,0,0), area 0.3mm2, adj f4,f255,f262,f265
  f265: sphere r=0.6mm, area 0mm2, adj f4,f263,f264
  f266: plane 9.97x6.83mm, normal (0,0,1), area 12.4mm2, adj f268,f269,f271,f273,f274,f275
  f267: sphere r=0.6mm, area 0mm2, adj f4,f268,f269
  f268: cylinder r=0.6mm len=1mm, axis (1,0,0), area 0.3mm2, adj f4,f266,f267,f270
  f269: cylinder r=0.6mm len=0.73mm, axis (0,1,0), area 0.2mm2, adj f4,f266,f267,f271
  f270: sphere r=0.6mm, area 0mm2, adj f4,f268,f273
  f271: torus R=9.67mm, axis (0,0,1), area 3.4mm2, adj f4,f266,f269,f272,f286,f288
  f272: sphere r=0.6mm, area 0.1mm2, adj f4,f271,f274,f280,f282,f284
  f273: cylinder r=0.6mm len=0.63mm, axis (0,-1,0), area 0.2mm2, adj f4,f266,f270,f275
  f274: cylinder r=0.6mm len=1.05mm, axis (0,1,0), area 0.3mm2, adj f4,f266,f272,f276
  f275: torus R=8.82mm, axis (0,0,1), area 2.9mm2, adj f4,f266,f273,f276
  f276: sphere r=0.6mm, area 0mm2, adj f4,f274,f275
  f277: cylinder r=0.3mm len=41.05mm, axis (1,0,0), area 19.3mm2, adj f4,f230,f278,f279
  f278: torus R=10.2mm, axis (0,0,1), area 1.5mm2, adj f4,f231,f277,f280
  f279: torus R=10.2mm, axis (0,0,1), area 1.5mm2, adj f0,f4,f277,f281
  f280: bspline ~0.31x0.3mm, area 0mm2, adj f231,f272,f278,f282
  f281: bspline ~0.32x0.31mm, area 0mm2, adj f0,f250,f279,f283
  f282: bspline ~0.33x0.3mm, area 0mm2, adj f22,f272,f280,f284
  f283: bspline ~0.34x0.34mm, area 0mm2, adj f36,f250,f281,f285
  f284: bspline ~0.29x0.28mm, area 0mm2, adj f23,f272,f282,f286
  f285: bspline ~0.29x0.28mm, area 0mm2, adj f37,f250,f283,f287
  f286: bspline ~7.36x6.99mm, area 3.9mm2, adj f23,f271,f284,f288
  f287: bspline ~7.36x6.99mm, area 3.9mm2, adj f37,f248,f285,f289
  f288: bspline ~0.73x0.44mm, area 0.3mm2, adj f1,f271,f286,f290
  f289: bspline ~0.73x0.44mm, area 0.3mm2, adj f228,f248,f287,f291
  f290: torus R=10.2mm, axis (0,0,1), area 1mm2, adj f1,f4,f288,f292
  f291: torus R=10.2mm, axis (0,0,1), area 1mm2, adj f228,f240,f289,f293
  f292: cylinder r=0.3mm len=98mm, axis (0,1,0), area 46.2mm2, adj f4,f83,f290,f294
  f293: cylinder r=0.3mm len=98mm, axis (0,1,0), area 46.2mm2, adj f86,f240,f291,f295
  f294: torus R=10.2mm, axis (0,0,1), area 1mm2, adj f4,f226,f292,f296
  f295: torus R=10.2mm, axis (0,0,1), area 1mm2, adj f2,f240,f293,f297
  f296: bspline ~0.73x0.44mm, area 0.3mm2, adj f226,f258,f294,f298
  f297: bspline ~0.73x0.44mm, area 0.3mm2, adj f2,f244,f295,f299
  f298: bspline ~7.36x6.99mm, area 3.9mm2, adj f40,f258,f296,f300
  f299: bspline ~7.36x6.99mm, area 3.9mm2, adj f43,f244,f297,f301
  f300: bspline ~0.29x0.28mm, area 0mm2, adj f40,f256,f298,f302
  f301: bspline ~0.29x0.28mm, area 0mm2, adj f43,f243,f299,f303
  f302: bspline ~0.34x0.34mm, area 0mm2, adj f44,f256,f300,f304
  f303: bspline ~0.33x0.3mm, area 0mm2, adj f49,f243,f301,f305
  f304: bspline ~0.32x0.31mm, area 0mm2, adj f3,f256,f302,f306
  f305: bspline ~0.31x0.3mm, area 0mm2, adj f227,f243,f303,f307
  f306: torus R=10.2mm, axis (0,0,1), area 1.5mm2, adj f3,f4,f304,f308
  f307: torus R=10.2mm, axis (0,0,1), area 1.5mm2, adj f4,f227,f305,f308
  f308: cylinder r=0.3mm len=41.05mm, axis (-1,0,0), area 19.3mm2, adj f4,f229,f306,f307
  f309: torus R=8.3mm, axis (0,0,1), area 6mm2, adj f4,f238,f310,f311
  f310: cylinder r=0.3mm len=97.8mm, axis (0,-1,0), area 46.1mm2, adj f4,f237,f309,f312
  f311: cylinder r=0.3mm len=40.85mm, axis (-1,0,0), area 19.3mm2, adj f4,f239,f309,f313
  f312: torus R=8.3mm, axis (0,0,1), area 6mm2, adj f4,f236,f310,f314
  f313: torus R=8.3mm, axis (0,0,1), area 6mm2, adj f4,f232,f311,f315
  f314: cylinder r=0.3mm len=40.85mm, axis (1,0,0), area 19.3mm2, adj f4,f235,f312,f316
  f315: cylinder r=0.3mm len=97.8mm, axis (0,1,0), area 46.1mm2, adj f4,f233,f313,f316
  f316: torus R=8.3mm, axis (0,0,1), area 6mm2, adj f4,f234,f314,f315
  f317: torus R=10.2mm, axis (0,0,1), area 1.3mm2, adj f0,f34,f241,f318
  f318: cylinder r=0.3mm len=41.05mm, axis (-1,0,0), area 19.3mm2, adj f230,f241,f317,f319
  f319: torus R=10.2mm, axis (0,0,1), area 1.3mm2, adj f24,f231,f241,f318
  f320: torus R=10.2mm, axis (0,0,1), area 1.3mm2, adj f51,f227,f241,f321
  f321: cylinder r=0.3mm len=41.05mm, axis (1,0,0), area 19.3mm2, adj f229,f241,f320,f322
  f322: torus R=10.2mm, axis (0,0,1), area 1.3mm2, adj f3,f50,f241,f321
  f323: cylinder r=0.3mm len=32.7mm, axis (0,-1,0), area 15.2mm2, adj f26,f35,f83,f241
PLACE A rot(axis=(-0.08,-0.42,-0.9),0deg) t=(6.12,15.19,3.26)mm
PLACE B rot(axis=(-0.08,-0.42,-0.9),0deg) t=(6.12,15.19,2.26)mm fixed
MATE fastened B.f140 <-> A.f1  axis (0,0,1) through (-17.04,4.81,3.26)mm
